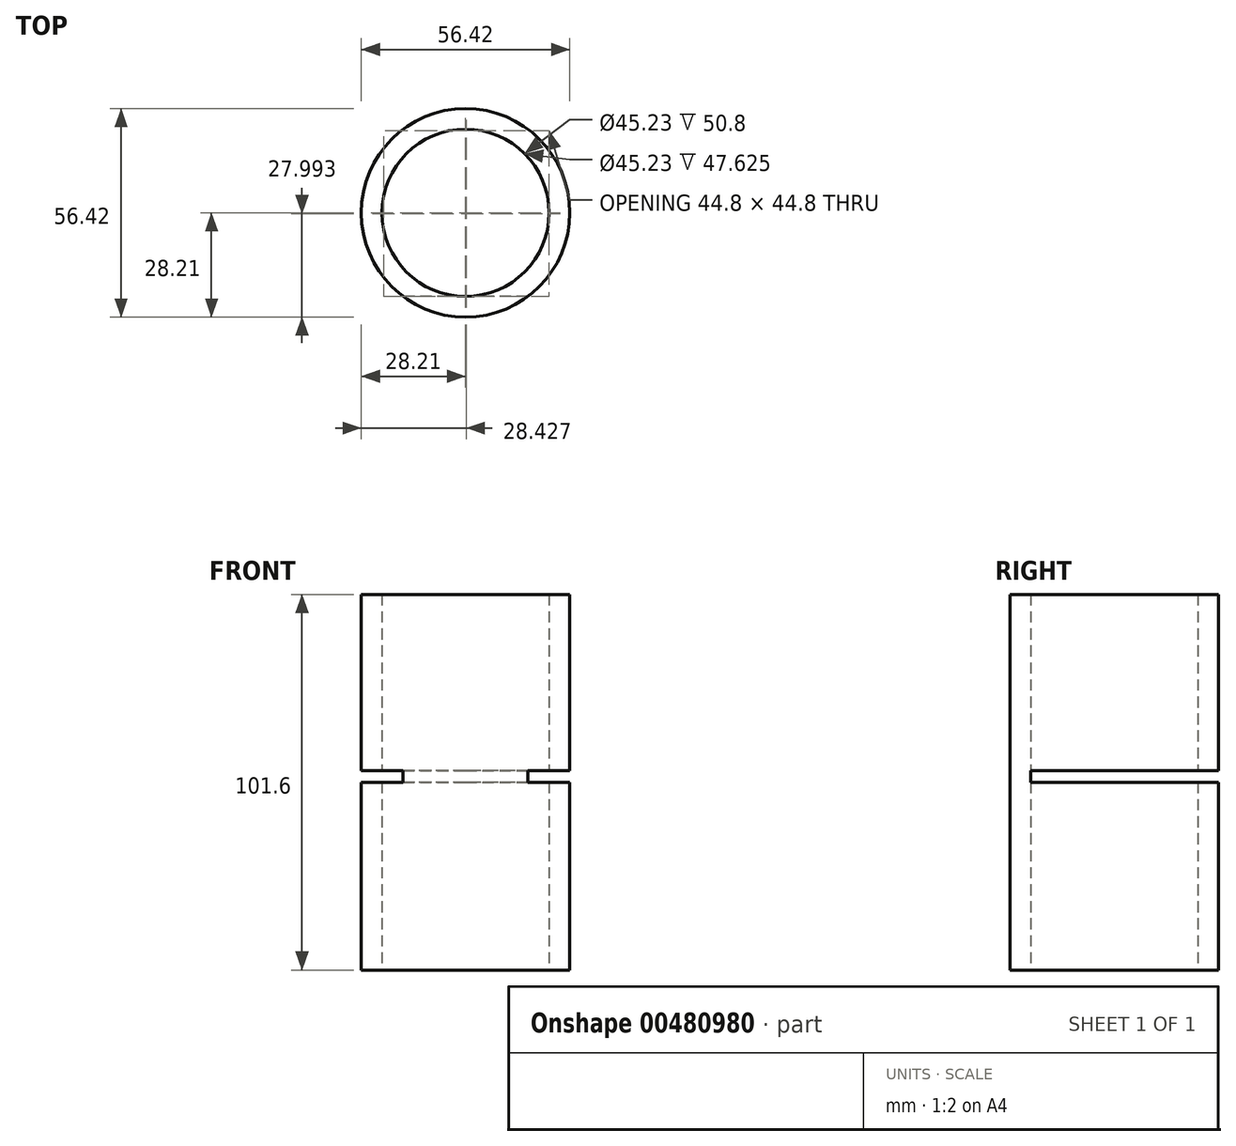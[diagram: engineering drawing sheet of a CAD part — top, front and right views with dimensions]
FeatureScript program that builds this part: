
annotation { "Feature Type Name" : "Feature", "Feature Type Description" : "" }
export const myFeature = defineFeature(function(context is Context, id is Id, definition is map)
    precondition{}
    {
        {
            var Q0;
            Q0=qCreatedBy(makeId("Top.planeOp"),FACE);
            var sketch = newSketch(context, id + "F0", { "sketchPlane" : qUnion([Q0])});
            skCircle(sketch, "E0", {"center": v(0, 0) * mm, "radius": 28.21 * mm});
            skCircle(sketch, "E1", {"center": v(0, 0) * mm, "radius": 22.62 * mm});
            skSolve(sketch);
        }
        {
            var Q0;
            Q0=makeQuery(id+"F0.imprint","IMPRINT",FACE,{"disambiguationData":[TD([[makeQuery(id+"F0.imprint","IMPRINT",EDGE,{"derivedFrom":sQuery(id+"F0.wireOp",EDGE,"E0")}),1.0]])]});
            extrude(context, id + "F1", {"entities" : qUnion([Q0]), "depth" : 101.6 * mm});
        }
        {
            var Q0;
            Q0=makeQuery(id+"F1.opExtrude","SWEPT_BODY",BODY,{"disambiguationData":[OSD([sQuery(id+"F0.wireOp",EDGE,"E0"),sQuery(id+"F0.wireOp",EDGE,"E1")])]});
            var Q1;
            Q1=qCreatedBy(makeId("Top.planeOp"),FACE);
            transform(context, id + "F2", {"entities" : qUnion([Q0]), "transformType" : TransformType.TRANSLATION_DISTANCE, "transformDirection" : qUnion([Q1]), "distance" : 50.8 * mm, "oppositeDirection" : true, "makeCopy" : false});
        }
        {
            var Q0;
            Q0=qCreatedBy(makeId("Top.planeOp"),FACE);
            var sketch = newSketch(context, id + "F3", { "sketchPlane" : qUnion([Q0])});
            skLineSegment(sketch, "E2.bottom", {"start": v(28.21, -22.62) * mm, "end": v(-28.21, -22.62) * mm});
            skLineSegment(sketch, "E2.top", {"start": v(28.21, 28.21) * mm, "end": v(-28.21, 28.21) * mm});
            skLineSegment(sketch, "E2.left", {"start": v(28.21, -22.62) * mm, "end": v(28.21, 28.21) * mm});
            skLineSegment(sketch, "E2.right", {"start": v(-28.21, -22.62) * mm, "end": v(-28.21, 28.21) * mm});
            skPoint(sketch, "E2.middle", {"position": v(0, 2.8) * mm});
            skSolve(sketch);
        }
        {
            var Q0;
            Q0=makeQuery(id+"F3.imprint","IMPRINT",FACE,{"disambiguationData":[TD([[makeQuery(id+"F3.imprint","IMPRINT",EDGE,{"derivedFrom":sQuery(id+"F3.wireOp",EDGE,"E2.bottom")}),-1.0]])]});
            extrude(context, id + "F4", {"entities" : qUnion([Q0]), "operationType" : NewBodyOperationType.REMOVE, "depth" : 3.17 * mm});
        }
    });
